# Revit family: CLASSEQ_C400
name_source: partatom
category: Specialty Equipment
units: mm (PartAtom-declared; Revit-internal decimal feet)

## family parameters
Always vertical = Yes
Cut with Voids When Loaded = No
OmniClass Number = 23.45.30.14
OmniClass Title = Commercial Washing Equipment
Part Type = Normal
Room Calculation Point = No
Round Connector Dimension = Use Diameter
Shared = No
Work Plane-Based = No

## types (2) — shared parameters
Amps Required (13A 1PH Set-up) = 13A (1 Phase)
Amps Required (13A 3PH Set-up) = 30A (1 phase)
Amps Required (20A 1PH Set-up) = 20A (1 Phase)
Amps Required (30A 1PH Set-up) = 30A (1 Phase)
BIMObjectName = C400
Clear Entry Height = 312 mm
Description = Undercounter Dishwasher
Dishwasher = QF_Stainless-Polished-Brushed
Door Depth (when Open) = 910 mm
Door Handle = QF_White_Colour
Door height (when Open) = 310 mm
Drain Flow rate = 20 L/min
Drain Size = Ø40 mm
DurationUnit = year
Glasses per Rack = 16
Height = 750 mm  [stored 2.46063 ft]
Length = 570 mm  [stored 1.87008 ft]
Manufacturer = CLASSEQ
ManufacturerName = CLASSEQ
ManufacturerURL = www.classeq.co.uk
Maximum Drain Height (from Machine Base) = 500 mm
Maximum Incoming Water temperature = 55˚C
Minimum Incoming Water temperature = 4˚C
Minimum allowed supply water pressure = 1 - 10 bar
Model = C400
NBSTypeID = 45-35-15/424 Commercial undercounter dishwashers
Operating Voltage (13A 1PH Set-up) = 220-240V /1N~ / 50Hz
Operating Voltage (13A 3PH Set-up) = 220-240V / 1N~ / 50Hz
Operating Voltage (20A 1PH Set-up) = 220-240V /1N~ / 50Hz
Operating Voltage (30A 1PH Set-up) = 220-240V / 1N~ / 50Hz
Phase = 1
ProductInformation = Undercounter Dishwasher
Required Water flow rate = 4 L/min
Revision = 1
Rinse Pump Input Power = 190 W
Rinse Tank Capacity = 6.5 litres
Rinse Tank Element (Standard) = 6.0 kW
Rinse tank Temperature (Dish) = 82˚C(default)
Rinse tank Temperature (Glass) = 70˚C(default)
Theoretical Max Rack per hour (1.5 / 2 min) Glass = 40/30
Theoretical Max Rack per hour (2 / 3 / 5 min) Dish = 30/20/12
Total Connected Load (13A 1PH Set-up) = 2.5 kW
Total Connected Load (13A 3PH Set-up) = 6.58 kW
Total Connected Load (20A 1PH Set-up) = 4.5 kW
Total Connected Load (30A 1PH Set-up) = 6.5 kW
Type Comments = Manufactured Product
URL = https://1drv.ms
Uniclass2015Code = Pr_40_70_21_92
Pr_40_70_21_92
Uniclass2015Title = Under-counter Dishwashers
Uniclass2015Version = v1.6
Version = 2021
Voltage = 220.00 V
Volts = 220 V
WarrantyDurationUnit = year
Wash Pump Input power = 450 W
Wash Tank Capacity = 9.5 litres
Wash Tank Element = 2.0 kW
Wash tank Temperature = 60˚C(default)
Water Supply connection = G3/4” (3/4” BSP)
Water consumption per cycle = 2.75 litres
Weight (Empty) = TBC
Weight (Full) = TBC
Weight (Packed) = TBC
Width = 460 mm  [stored 1.50919 ft]
zero-valued in all types: Default Elevation

## per-type parameters (varying)
| type | Inbuilt Water softener option |
| C400 | No |
| C400 WS | Yes |

note: [stored X ft] marks values corroborated as IEEE doubles in the binary element streams (Revit-internal decimal feet)

## geometry (parser evidence)
native form markers: Sweep x8
no freeform markers — native parametric forms only
